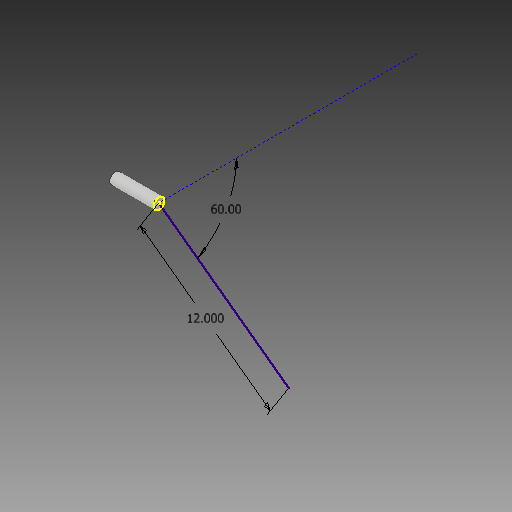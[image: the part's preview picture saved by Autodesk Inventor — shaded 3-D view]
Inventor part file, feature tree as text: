
AUTODESK INVENTOR PART (.ipt)
format: ipt  version: 2019 (Build 230136000, 136)  size: 96,256 bytes
history: native  units: in
note: dims shown in document units (in); Inventor stores cm internally (conversion verified against a paired STEP export)
features: sketch x2, extrude x1
ambient origin geometry x8: Origin, YZ Plane, XZ Plane, XY Plane, X Axis, Y Axis, Z Axis, Center Point
bodies: Solid1 (feature_tree)
feature tree (3):
  extrude  "Extrusion1"  Depth=2.0in TaperAngle=0.0deg
  sketch  "Sketch2"  dims[d3=12.0in d4=60.0deg]
  sketch  "Sketch1"  dims[d0=0.5in d1=2.0in d2=0.0in]
